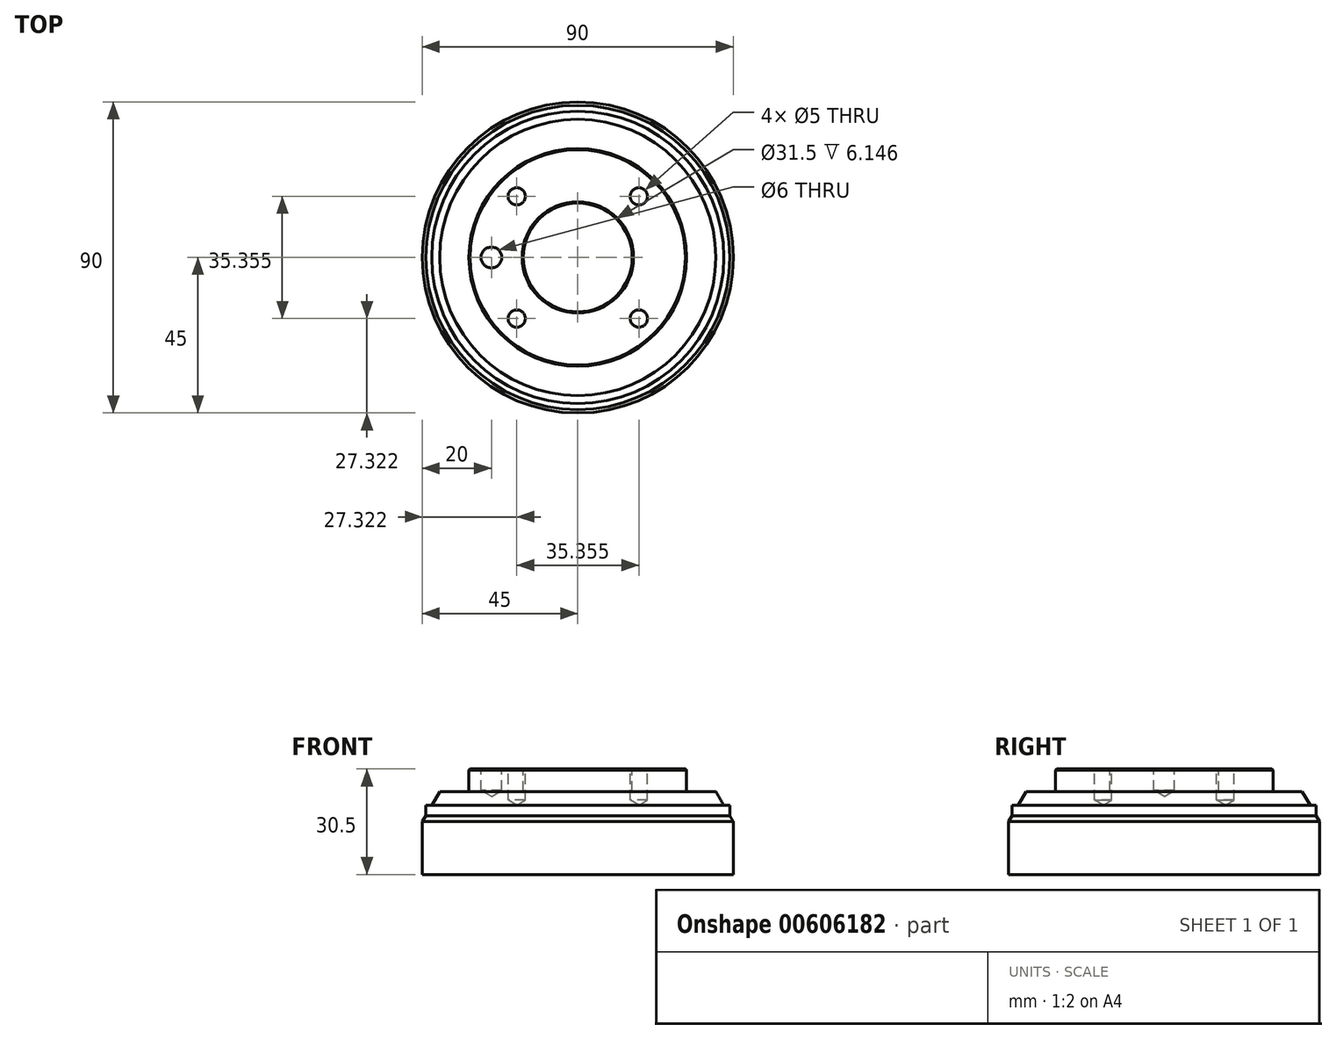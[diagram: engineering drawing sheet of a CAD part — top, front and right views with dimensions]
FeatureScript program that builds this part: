
annotation { "Feature Type Name" : "Feature", "Feature Type Description" : "" }
export const myFeature = defineFeature(function(context is Context, id is Id, definition is map)
    precondition{}
    {
        {
            var Q0;
            Q0=qCreatedBy(makeId("Front.planeOp"),FACE);
            var sketch = newSketch(context, id + "F0", { "sketchPlane" : qUnion([Q0])});
            skLineSegment(sketch, "E0", {"start": v(0, 0) * mm, "end": v(45, 0) * mm});
            skLineSegment(sketch, "E1", {"start": v(45, 0) * mm, "end": v(45, 15.27) * mm});
            skLineSegment(sketch, "E2", {"start": v(45, 15.27) * mm, "end": v(44, 17) * mm});
            skLineSegment(sketch, "E3", {"start": v(44, 17) * mm, "end": v(44, 20) * mm});
            skLineSegment(sketch, "E4", {"start": v(44, 20) * mm, "end": v(42.27, 20) * mm});
            skLineSegment(sketch, "E5", {"start": v(42.27, 20) * mm, "end": v(39.96, 24) * mm});
            skLineSegment(sketch, "E6", {"start": v(39.96, 24) * mm, "end": v(31.5, 24) * mm});
            skLineSegment(sketch, "E7", {"start": v(31.5, 24) * mm, "end": v(31.5, 30.15) * mm});
            skLineSegment(sketch, "E8", {"start": v(31.5, 30.15) * mm, "end": v(31.15, 30.5) * mm});
            skLineSegment(sketch, "E9", {"start": v(31.15, 30.5) * mm, "end": v(16.1, 30.5) * mm});
            skLineSegment(sketch, "E10", {"start": v(16.1, 30.5) * mm, "end": v(15.75, 30.15) * mm});
            skLineSegment(sketch, "E11", {"start": v(15.75, 30.15) * mm, "end": v(15.75, 24) * mm});
            skLineSegment(sketch, "E12", {"start": v(15.75, 24) * mm, "end": v(0, 24) * mm});
            skLineSegment(sketch, "E13", {"start": v(0, 24) * mm, "end": v(0, 0) * mm});
            skSolve(sketch);
        }
        {
            var Q0;
            Q0 = qSketchRegion(id + "F0", true);
            var Q1;
            Q1=sQuery(id+"F0.wireOp",EDGE,"E13");
            revolve(context, id + "F1", {"entities" : qUnion([Q0]), "axis" : qUnion([Q1]), "revolveType" : RevolveType.FULL});
        }
        {
            var Q0;
            Q0=makeQuery(id+"F1.opRevolve","SWEPT_FACE",FACE,{"disambiguationData":[OSD([sQuery(id+"F0.wireOp",EDGE,"E9")])]});
            var sketch = newSketch(context, id + "F2", { "sketchPlane" : qUnion([Q0])});
            skCircle(sketch, "E14", {"center": v(0, 0) * mm, "radius": 25 * mm, "construction": true});
            skPoint(sketch, "E15", {"position": v(-17.68, 17.68) * mm});
            skPoint(sketch, "E16", {"position": v(17.68, 17.68) * mm});
            skPoint(sketch, "E17", {"position": v(17.68, -17.68) * mm});
            skPoint(sketch, "E18", {"position": v(-17.68, -17.68) * mm});
            skLineSegment(sketch, "E19", {"start": v(-17.68, 17.68) * mm, "end": v(17.68, -17.68) * mm, "construction": true});
            skLineSegment(sketch, "E20", {"start": v(17.68, 17.68) * mm, "end": v(-17.68, -17.68) * mm, "construction": true});
            skPoint(sketch, "E21", {"position": v(-25, 0) * mm});
            skSolve(sketch);
        }
        {
            var Q0;
            Q0=sQuery(id+"F2.wireOp",VERTEX,"E15");
            var Q1;
            Q1=sQuery(id+"F2.wireOp",VERTEX,"E18");
            var Q2;
            Q2=sQuery(id+"F2.wireOp",VERTEX,"E16");
            var Q3;
            Q3=sQuery(id+"F2.wireOp",VERTEX,"E17");
            var Q4;
            Q4=makeQuery(id+"F1.opRevolve","SWEPT_BODY",BODY,{"disambiguationData":[OSD([sQuery(id+"F0.wireOp",EDGE,"E0"),sQuery(id+"F0.wireOp",EDGE,"E1"),sQuery(id+"F0.wireOp",EDGE,"E2"),sQuery(id+"F0.wireOp",EDGE,"E3"),sQuery(id+"F0.wireOp",EDGE,"E4"),sQuery(id+"F0.wireOp",EDGE,"E5"),sQuery(id+"F0.wireOp",EDGE,"E6"),sQuery(id+"F0.wireOp",EDGE,"E7"),sQuery(id+"F0.wireOp",EDGE,"E8"),sQuery(id+"F0.wireOp",EDGE,"E9"),sQuery(id+"F0.wireOp",EDGE,"E10"),sQuery(id+"F0.wireOp",EDGE,"E11"),sQuery(id+"F0.wireOp",EDGE,"E12"),sQuery(id+"F0.wireOp",EDGE,"E13")])]});
            hole(context, id + "F3", {"style" : HoleStyle.SIMPLE, "endStyle" : HoleEndStyle.BLIND, "standardTappedOrClearance" : lookupTablePath({ "standard" : "ISO", "engagement" : "75%", "pitch" : "1 mm", "size" : "M6", "type" : "Tapped" }), "standardBlindInLast" : lookupTablePath({ "standard" : "ISO", "engagement" : "75%", "pitch" : "1 mm", "size" : "M6", "type" : "Tapped" }), "holeDiameter" : 5 * mm, "majorDiameter" : 6 * mm, "showTappedDepth" : true, "holeDepth" : 9 * mm, "isTappedThrough" : true, "tappedDepth" : 6 * mm, "tapClearance" : 3, "startFromSketch" : true, "locations" : qUnion([Q0, Q1, Q2, Q3]), "scope" : qUnion([Q4])});
        }
        {
            var Q0;
            Q0=sQuery(id+"F2.wireOp",VERTEX,"E21");
            var Q1;
            Q1=makeQuery(id+"F1.opRevolve","SWEPT_BODY",BODY,{"disambiguationData":[OSD([sQuery(id+"F0.wireOp",EDGE,"E0"),sQuery(id+"F0.wireOp",EDGE,"E1"),sQuery(id+"F0.wireOp",EDGE,"E2"),sQuery(id+"F0.wireOp",EDGE,"E3"),sQuery(id+"F0.wireOp",EDGE,"E4"),sQuery(id+"F0.wireOp",EDGE,"E5"),sQuery(id+"F0.wireOp",EDGE,"E6"),sQuery(id+"F0.wireOp",EDGE,"E7"),sQuery(id+"F0.wireOp",EDGE,"E8"),sQuery(id+"F0.wireOp",EDGE,"E9"),sQuery(id+"F0.wireOp",EDGE,"E10"),sQuery(id+"F0.wireOp",EDGE,"E11"),sQuery(id+"F0.wireOp",EDGE,"E12"),sQuery(id+"F0.wireOp",EDGE,"E13")])]});
            hole(context, id + "F4", {"style" : HoleStyle.SIMPLE, "endStyle" : HoleEndStyle.BLIND, "standardTappedOrClearance" : lookupTablePath({ "standard" : "ISO", "size" : "6", "type" : "Drilled" }), "standardBlindInLast" : lookupTablePath({ "standard" : "ISO", "size" : "6", "type" : "Drilled" }), "holeDiameter" : 6 * mm, "majorDiameter" : 6 * mm, "holeDepth" : 6.2 * mm, "isTappedThrough" : true, "tappedDepth" : 6 * mm, "tapClearance" : 3, "startFromSketch" : true, "locations" : qUnion([Q0]), "scope" : qUnion([Q1])});
        }
    });
